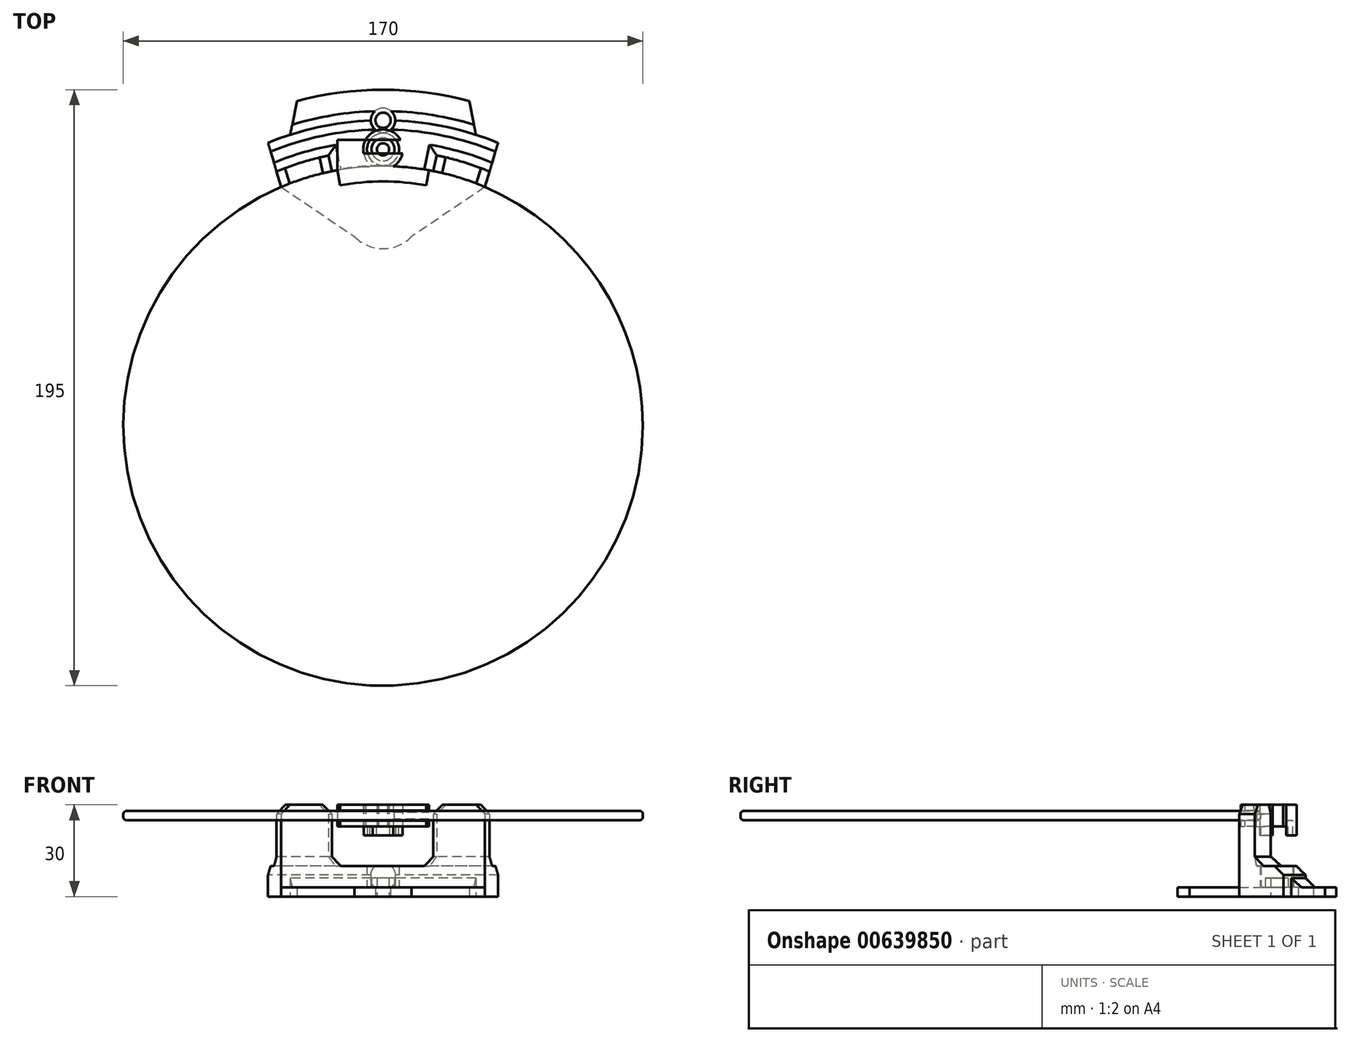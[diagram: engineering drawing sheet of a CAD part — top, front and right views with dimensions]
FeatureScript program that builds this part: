
annotation { "Feature Type Name" : "Feature", "Feature Type Description" : "" }
export const myFeature = defineFeature(function(context is Context, id is Id, definition is map)
    precondition{}
    {
        {
            var Q0;
            Q0=qCreatedBy(makeId("Top.planeOp"),FACE);
            var sketch = newSketch(context, id + "F0", { "sketchPlane" : qUnion([Q0])});
            skCircle(sketch, "E0", {"center": v(0, 0) * mm, "radius": 85 * mm});
            skLineSegment(sketch, "E1", {"start": v(0, 85) * mm, "end": v(0, 0) * mm, "construction": true});
            skLineSegment(sketch, "E2", {"start": v(0, 0) * mm, "end": v(-73.61, -42.5) * mm, "construction": true});
            skLineSegment(sketch, "E3", {"start": v(0, 0) * mm, "end": v(73.61, -42.5) * mm, "construction": true});
            skCircle(sketch, "E4", {"center": v(0, 100) * mm, "radius": 2.5 * mm});
            skCircle(sketch, "E5", {"center": v(0, 0) * mm, "radius": 100 * mm});
            skCircle(sketch, "E6", {"center": v(0, 0) * mm, "radius": 110 * mm});
            skCircle(sketch, "E7", {"center": v(0, 100) * mm, "radius": 4 * mm});
            skCircle(sketch, "E8", {"center": v(0, 71) * mm, "radius": 13 * mm});
            skCircle(sketch, "E9", {"center": v(0, 71) * mm, "radius": 9.5 * mm});
            skLineSegment(sketch, "E10", {"start": v(-37.65, 92.64) * mm, "end": v(-33.33, 78.2) * mm});
            skLineSegment(sketch, "E11", {"start": v(-33.33, 78.2) * mm, "end": v(-9.32, 61.94) * mm});
            skLineSegment(sketch, "E12", {"start": v(-30.4, 95.27) * mm, "end": v(-28.21, 106.32) * mm});
            skLineSegment(sketch, "E13.MirrorCS", {"start": v(33.33, 78.2) * mm, "end": v(9.32, 61.94) * mm});
            skLineSegment(sketch, "E14.MirrorCS", {"start": v(37.65, 92.64) * mm, "end": v(33.33, 78.2) * mm});
            skLineSegment(sketch, "E15.MirrorCS", {"start": v(30.4, 95.27) * mm, "end": v(28.21, 106.32) * mm});
            skArc(sketch, "E16", {"start": v(34.84, 83.25) * mm, "mid": v(0, 90.24) * mm, "end": v(-34.84, 83.25) * mm});
            skLineSegment(sketch, "E17", {"start": v(17.54, 88.52) * mm, "end": v(16.45, 83.4) * mm});
            skLineSegment(sketch, "E18", {"start": v(0, 85) * mm, "end": v(0, 116.4) * mm, "construction": true});
            skLineSegment(sketch, "E19", {"start": v(-17.83, 88.46) * mm, "end": v(-16.74, 83.33) * mm});
            skSolve(sketch);
        }
        {
            var Q0;
            {var subQ4=sQuery(id+"F0.wireOp",EDGE,"E12");Q0=makeQuery(id+"F0.imprint","IMPRINT",FACE,{"disambiguationData":[TD([[makeQuery(id+"F0.imprint","IMPRINT",EDGE,{"derivedFrom":subQ4}),-1.0]])]});}
            var Q1;
            {var subQ0=sQuery(id+"F0.wireOp",EDGE,"E5");var subQ1=sQuery(id+"F0.wireOp",EDGE,"E4");var subQ2=makeQuery(id+"F0.imprint","INTERSECT",VERTEX,{"disambiguationData":[OD(0.0)],"derivedFrom":[subQ1,subQ0]});Q1=makeQuery(id+"F0.imprint","IMPRINT",FACE,{"disambiguationData":[TD([[makeQuery(id+"F0.imprint","IMPRINT",EDGE,{"disambiguationData":[TD([[subQ2,-1.0]])],"derivedFrom":subQ1}),-1.0]])]});}
            var Q2;
            {var subQ0=sQuery(id+"F0.wireOp",EDGE,"E5");var subQ1=sQuery(id+"F0.wireOp",EDGE,"E4");var subQ2=makeQuery(id+"F0.imprint","INTERSECT",VERTEX,{"disambiguationData":[OD(0.0)],"derivedFrom":[subQ1,subQ0]});Q2=makeQuery(id+"F0.imprint","IMPRINT",FACE,{"disambiguationData":[TD([[makeQuery(id+"F0.imprint","IMPRINT",EDGE,{"disambiguationData":[TD([[subQ2,1.0]])],"derivedFrom":subQ1}),-1.0]])]});}
            var Q3;
            {var subQ7=sQuery(id+"F0.wireOp",EDGE,"E10");Q3=makeQuery(id+"F0.imprint","IMPRINT",FACE,{"disambiguationData":[TD([[makeQuery(id+"F0.imprint","IMPRINT",EDGE,{"derivedFrom":subQ7}),1.0]])]});}
            var Q4;
            {var subQ0=sQuery(id+"F0.wireOp",EDGE,"E11");Q4=makeQuery(id+"F0.imprint","IMPRINT",FACE,{"disambiguationData":[TD([[makeQuery(id+"F0.imprint","IMPRINT",EDGE,{"derivedFrom":subQ0}),1.0]])]});}
            var Q5;
            Q5=makeQuery(id+"F0.imprint","IMPRINT",FACE,{"disambiguationData":[TD([[makeQuery(id+"F0.imprint","IMPRINT",EDGE,{"derivedFrom":sQuery(id+"F0.wireOp",EDGE,"E9")}),-1.0]])]});
            var Q6;
            Q6=makeQuery(id+"F0.imprint","IMPRINT",FACE,{"disambiguationData":[TD([[makeQuery(id+"F0.imprint","IMPRINT",EDGE,{"derivedFrom":sQuery(id+"F0.wireOp",EDGE,"E9")}),1.0]])]});
            var Q7;
            {var subQ7=sQuery(id+"F0.wireOp",EDGE,"E16");Q7=makeQuery(id+"F0.imprint","IMPRINT",FACE,{"disambiguationData":[TD([[makeQuery(id+"F0.imprint","IMPRINT",EDGE,{"derivedFrom":subQ7}),-1.0]])]});}
            extrude(context, id + "F1", {"entities" : qUnion([Q0, Q1, Q2, Q3, Q4, Q5, Q6, Q7]), "depth" : 3 * mm, "offsetDistance" : 25 * mm});
        }
        {
            var Q0;
            {var subQ7=sQuery(id+"F0.wireOp",EDGE,"E10");Q0=makeQuery(id+"F0.imprint","IMPRINT",FACE,{"disambiguationData":[TD([[makeQuery(id+"F0.imprint","IMPRINT",EDGE,{"derivedFrom":subQ7}),1.0]])]});}
            var Q1;
            {var subQ7=sQuery(id+"F0.wireOp",EDGE,"E16");Q1=makeQuery(id+"F0.imprint","IMPRINT",FACE,{"disambiguationData":[TD([[makeQuery(id+"F0.imprint","IMPRINT",EDGE,{"derivedFrom":subQ7}),-1.0]])]});}
            var Q2;
            {var subQ0=sQuery(id+"F0.wireOp",EDGE,"E17");Q2=makeQuery(id+"F0.imprint","IMPRINT",FACE,{"disambiguationData":[TD([[makeQuery(id+"F0.imprint","IMPRINT",EDGE,{"derivedFrom":subQ0}),-1.0]])]});}
            var Q3;
            {var subQ3=sQuery(id+"F0.wireOp",EDGE,"E17");Q3=makeQuery(id+"F0.imprint","IMPRINT",FACE,{"disambiguationData":[TD([[makeQuery(id+"F0.imprint","IMPRINT",EDGE,{"derivedFrom":subQ3}),1.0]])]});}
            extrude(context, id + "F2", {"entities" : qUnion([Q0, Q1, Q2, Q3]), "operationType" : NewBodyOperationType.ADD, "depth" : 10 * mm, "offsetDistance" : 25 * mm});
        }
        {
            var Q0;
            {var subQ3=sQuery(id+"F0.wireOp",EDGE,"E17");Q0=makeQuery(id+"F0.imprint","IMPRINT",FACE,{"disambiguationData":[TD([[makeQuery(id+"F0.imprint","IMPRINT",EDGE,{"derivedFrom":subQ3}),1.0]])]});}
            var Q1;
            {var subQ3=sQuery(id+"F0.wireOp",EDGE,"E19");Q1=makeQuery(id+"F0.imprint","IMPRINT",FACE,{"disambiguationData":[TD([[makeQuery(id+"F0.imprint","IMPRINT",EDGE,{"derivedFrom":subQ3}),-1.0]])]});}
            extrude(context, id + "F3", {"entities" : qUnion([Q0, Q1]), "operationType" : NewBodyOperationType.ADD, "depth" : 30 * mm, "offsetDistance" : 25 * mm});
        }
        {
            var Q0;
            Q0=qCreatedBy(makeId("Top.planeOp"),FACE);
            cPlane(context, id + "F4", {"entities" : qUnion([Q0]), "cplaneType" : CPlaneType.OFFSET, "offset" : 25 * mm, "width" : 150 * mm, "height" : 150 * mm});
        }
        {
            var Q0;
            Q0=qCreatedBy(id+"F4.planeOp",FACE);
            var sketch = newSketch(context, id + "F5", { "sketchPlane" : qUnion([Q0])});
            skLineSegment(sketch, "E20.top", {"start": v(15, 89.17) * mm, "end": v(-15, 89.17) * mm});
            skPoint(sketch, "E20.middle", {"position": v(0, 85) * mm});
            skArc(sketch, "E21", {"start": v(15, 83.67) * mm, "mid": v(0, 85) * mm, "end": v(-15, 83.67) * mm});
            skArc(sketch, "E22", {"start": v(-15, 83.67) * mm, "mid": v(0, -85) * mm, "end": v(15, 83.67) * mm});
            skLineSegment(sketch, "E23.bottom", {"start": v(-15, 89.17) * mm, "end": v(14.83, 89.17) * mm});
            skLineSegment(sketch, "E23.top", {"start": v(-15, 93.56) * mm, "end": v(14.83, 93.56) * mm});
            skLineSegment(sketch, "E23.left", {"start": v(-15, 89.17) * mm, "end": v(-15, 93.56) * mm});
            skArc(sketch, "E24.0", {"start": v(14.12, 78.74) * mm, "mid": v(0, 80) * mm, "end": v(-14.12, 78.74) * mm});
            skLineSegment(sketch, "E25", {"start": v(-15, 89.17) * mm, "end": v(-15, 83.67) * mm});
            skLineSegment(sketch, "E26", {"start": v(-15, 83.67) * mm, "end": v(-14.12, 78.74) * mm});
            skLineSegment(sketch, "E27", {"start": v(14.12, 78.74) * mm, "end": v(15, 83.67) * mm});
            skLineSegment(sketch, "E28", {"start": v(15, 83.67) * mm, "end": v(15, 89.17) * mm});
            skLineSegment(sketch, "E29", {"start": v(0, 85) * mm, "end": v(0, 93.56) * mm, "construction": true});
            skPoint(sketch, "E29.endSnap0", {"position": v(0, 89.17) * mm});
            skLineSegment(sketch, "E30", {"start": v(14.83, 93.56) * mm, "end": v(15, 93.56) * mm});
            skLineSegment(sketch, "E31", {"start": v(15, 93.56) * mm, "end": v(15, 89.17) * mm});
            skCircle(sketch, "E32", {"center": v(0, 90.5) * mm, "radius": 5.25 * mm});
            skCircle(sketch, "E33", {"center": v(0, 90.5) * mm, "radius": 3.75 * mm});
            skCircle(sketch, "E34", {"center": v(0, 90.5) * mm, "radius": 2 * mm});
            skArc(sketch, "E35", {"start": v(5.74, 93.56) * mm, "mid": v(0, 97) * mm, "end": v(-5.74, 93.56) * mm});
            skArc(sketch, "E36", {"start": v(-5.74, 93.56) * mm, "mid": v(0, 84) * mm, "end": v(5.74, 93.56) * mm});
            skSolve(sketch);
        }
        {
            var Q0;
            Q0=makeQuery(id+"F5.imprint","IMPRINT",FACE,{"disambiguationData":[TD([[makeQuery(id+"F5.imprint","IMPRINT",EDGE,{"derivedFrom":sQuery(id+"F5.wireOp",EDGE,"E22")}),1.0]])]});
            var Q1;
            Q1=makeQuery(id+"F5.imprint","IMPRINT",FACE,{"disambiguationData":[TD([[makeQuery(id+"F5.imprint","IMPRINT",EDGE,{"derivedFrom":sQuery(id+"F5.wireOp",EDGE,"E21")}),1.0]])]});
            var Q2;
            {var subQ0=sQuery(id+"F5.wireOp",EDGE,"E36");var subQ1=sQuery(id+"F5.wireOp",EDGE,"E21");var subQ2=makeQuery(id+"F5.imprint","INTERSECT",VERTEX,{"disambiguationData":[OD(0.0)],"derivedFrom":[subQ1,subQ0]});Q2=makeQuery(id+"F5.imprint","IMPRINT",FACE,{"disambiguationData":[TD([[makeQuery(id+"F5.imprint","IMPRINT",EDGE,{"disambiguationData":[TD([[subQ2,-1.0]])],"derivedFrom":subQ1}),1.0]])]});}
            extrude(context, id + "F6", {"entities" : qUnion([Q0, Q1, Q2]), "depth" : 3 * mm, "offsetDistance" : 25 * mm});
        }
        {
            var Q0;
            Q0=makeQuery(id+"F6.opExtrude","SWEPT_FACE",FACE,{"disambiguationData":[OSD([sQuery(id+"F5.wireOp",EDGE,"E21"),sQuery(id+"F5.wireOp",EDGE,"E22")])]});
            fillet(context, id + "F7", {"entities" : qUnion([Q0]), "radius" : 1 * mm, "tangentPropagation" : true, "allowEdgeOverflow" : false});
        }
        {
            var Q0;
            {var subQ0=sQuery(id+"F5.wireOp",EDGE,"E23.left");Q0=makeQuery(id+"F5.imprint","IMPRINT",FACE,{"disambiguationData":[TD([[makeQuery(id+"F5.imprint","IMPRINT",EDGE,{"derivedFrom":subQ0}),-1.0]])]});}
            var Q1;
            {var subQ0=sQuery(id+"F5.wireOp",EDGE,"E32");var subQ1=sQuery(id+"F5.wireOp",EDGE,"E23.bottom");var subQ2=makeQuery(id+"F5.imprint","INTERSECT",VERTEX,{"disambiguationData":[OD(0.0)],"derivedFrom":[subQ1,subQ0]});Q1=makeQuery(id+"F5.imprint","IMPRINT",FACE,{"disambiguationData":[TD([[makeQuery(id+"F5.imprint","IMPRINT",EDGE,{"disambiguationData":[TD([[subQ2,-1.0]])],"derivedFrom":subQ1}),1.0]])]});}
            var Q2;
            {var subQ0=sQuery(id+"F5.wireOp",EDGE,"E33");var subQ1=sQuery(id+"F5.wireOp",EDGE,"E23.bottom");var subQ2=makeQuery(id+"F5.imprint","INTERSECT",VERTEX,{"disambiguationData":[OD(1.0)],"derivedFrom":[subQ1,subQ0]});Q2=makeQuery(id+"F5.imprint","IMPRINT",FACE,{"disambiguationData":[TD([[makeQuery(id+"F5.imprint","IMPRINT",EDGE,{"disambiguationData":[TD([[subQ2,-1.0]])],"derivedFrom":subQ1}),1.0]])]});}
            var Q3;
            Q3=makeQuery(id+"F5.imprint","IMPRINT",FACE,{"disambiguationData":[TD([[makeQuery(id+"F5.imprint","IMPRINT",EDGE,{"derivedFrom":sQuery(id+"F5.wireOp",EDGE,"E21")}),1.0]])]});
            var Q4;
            {var subQ0=sQuery(id+"F5.wireOp",EDGE,"E32");var subQ1=sQuery(id+"F5.wireOp",EDGE,"E23.bottom");var subQ2=makeQuery(id+"F5.imprint","INTERSECT",VERTEX,{"disambiguationData":[OD(0.0)],"derivedFrom":[subQ1,subQ0]});Q4=makeQuery(id+"F5.imprint","IMPRINT",FACE,{"disambiguationData":[TD([[makeQuery(id+"F5.imprint","IMPRINT",EDGE,{"disambiguationData":[TD([[subQ2,-1.0]])],"derivedFrom":subQ1}),-1.0]])]});}
            var Q5;
            {var subQ5=sQuery(id+"F5.wireOp",EDGE,"E20.top");Q5=makeQuery(id+"F5.imprint","IMPRINT",FACE,{"disambiguationData":[TD([[makeQuery(id+"F5.imprint","IMPRINT",EDGE,{"derivedFrom":subQ5}),-1.0]])]});}
            var Q6;
            {var subQ1=sQuery(id+"F5.wireOp",EDGE,"E20.top");Q6=makeQuery(id+"F5.imprint","IMPRINT",FACE,{"disambiguationData":[TD([[makeQuery(id+"F5.imprint","IMPRINT",EDGE,{"derivedFrom":subQ1}),1.0]])]});}
            var Q7;
            {var subQ0=sQuery(id+"F5.wireOp",EDGE,"E32");var subQ1=sQuery(id+"F5.wireOp",EDGE,"E23.top");var subQ2=makeQuery(id+"F5.imprint","INTERSECT",VERTEX,{"disambiguationData":[OD(0.0)],"derivedFrom":[subQ1,subQ0]});Q7=makeQuery(id+"F5.imprint","IMPRINT",FACE,{"disambiguationData":[TD([[makeQuery(id+"F5.imprint","IMPRINT",EDGE,{"disambiguationData":[TD([[subQ2,-1.0]])],"derivedFrom":subQ1}),1.0]])]});}
            var Q8;
            {var subQ0=sQuery(id+"F5.wireOp",EDGE,"E33");var subQ1=sQuery(id+"F5.wireOp",EDGE,"E23.bottom");var subQ2=makeQuery(id+"F5.imprint","INTERSECT",VERTEX,{"disambiguationData":[OD(0.0)],"derivedFrom":[subQ1,subQ0]});Q8=makeQuery(id+"F5.imprint","IMPRINT",FACE,{"disambiguationData":[TD([[makeQuery(id+"F5.imprint","IMPRINT",EDGE,{"disambiguationData":[TD([[subQ2,-1.0]])],"derivedFrom":subQ1}),1.0]])]});}
            var Q9;
            {var subQ0=sQuery(id+"F5.wireOp",EDGE,"E33");var subQ1=sQuery(id+"F5.wireOp",EDGE,"E23.bottom");var subQ2=makeQuery(id+"F5.imprint","INTERSECT",VERTEX,{"disambiguationData":[OD(0.0)],"derivedFrom":[subQ1,subQ0]});Q9=makeQuery(id+"F5.imprint","IMPRINT",FACE,{"disambiguationData":[TD([[makeQuery(id+"F5.imprint","IMPRINT",EDGE,{"disambiguationData":[TD([[subQ2,-1.0]])],"derivedFrom":subQ1}),-1.0]])]});}
            var Q10;
            {var subQ0=sQuery(id+"F5.wireOp",EDGE,"E33");var subQ1=sQuery(id+"F5.wireOp",EDGE,"E23.top");var subQ2=makeQuery(id+"F5.imprint","INTERSECT",VERTEX,{"disambiguationData":[OD(0.0)],"derivedFrom":[subQ1,subQ0]});Q10=makeQuery(id+"F5.imprint","IMPRINT",FACE,{"disambiguationData":[TD([[makeQuery(id+"F5.imprint","IMPRINT",EDGE,{"disambiguationData":[TD([[subQ2,-1.0]])],"derivedFrom":subQ1}),1.0]])]});}
            var Q11;
            {var subQ0=sQuery(id+"F5.wireOp",EDGE,"E35");Q11=makeQuery(id+"F5.imprint","IMPRINT",FACE,{"disambiguationData":[TD([[makeQuery(id+"F5.imprint","IMPRINT",EDGE,{"derivedFrom":subQ0}),1.0]])]});}
            var Q12;
            {var subQ0=sQuery(id+"F5.wireOp",EDGE,"E25");Q12=makeQuery(id+"F5.imprint","IMPRINT",FACE,{"disambiguationData":[TD([[makeQuery(id+"F5.imprint","IMPRINT",EDGE,{"derivedFrom":subQ0}),1.0]])]});}
            var Q13;
            {var subQ0=sQuery(id+"F5.wireOp",EDGE,"E36");var subQ1=sQuery(id+"F5.wireOp",EDGE,"E21");var subQ2=makeQuery(id+"F5.imprint","INTERSECT",VERTEX,{"disambiguationData":[OD(0.0)],"derivedFrom":[subQ1,subQ0]});Q13=makeQuery(id+"F5.imprint","IMPRINT",FACE,{"disambiguationData":[TD([[makeQuery(id+"F5.imprint","IMPRINT",EDGE,{"disambiguationData":[TD([[subQ2,-1.0]])],"derivedFrom":subQ1}),1.0]])]});}
            var Q14;
            {var subQ4=sQuery(id+"F5.wireOp",EDGE,"E36");var subQ7=sQuery(id+"F5.wireOp",EDGE,"E21");var subQ8=makeQuery(id+"F5.imprint","INTERSECT",VERTEX,{"disambiguationData":[OD(0.0)],"derivedFrom":[subQ7,subQ4]});Q14=makeQuery(id+"F5.imprint","IMPRINT",FACE,{"disambiguationData":[TD([[makeQuery(id+"F5.imprint","IMPRINT",EDGE,{"disambiguationData":[TD([[subQ8,-1.0]])],"derivedFrom":subQ7}),-1.0]])]});}
            var Q15;
            {var subQ0=sQuery(id+"F5.wireOp",EDGE,"E36");var subQ1=sQuery(id+"F5.wireOp",EDGE,"E23.bottom");var subQ2=makeQuery(id+"F5.imprint","INTERSECT",VERTEX,{"disambiguationData":[OD(0.0)],"derivedFrom":[subQ1,subQ0]});Q15=makeQuery(id+"F5.imprint","IMPRINT",FACE,{"disambiguationData":[TD([[makeQuery(id+"F5.imprint","IMPRINT",EDGE,{"disambiguationData":[TD([[subQ2,-1.0]])],"derivedFrom":subQ1}),1.0]])]});}
            var Q16;
            {var subQ0=sQuery(id+"F5.wireOp",EDGE,"E32");var subQ1=sQuery(id+"F5.wireOp",EDGE,"E23.bottom");var subQ2=makeQuery(id+"F5.imprint","INTERSECT",VERTEX,{"disambiguationData":[OD(1.0)],"derivedFrom":[subQ1,subQ0]});Q16=makeQuery(id+"F5.imprint","IMPRINT",FACE,{"disambiguationData":[TD([[makeQuery(id+"F5.imprint","IMPRINT",EDGE,{"disambiguationData":[TD([[subQ2,-1.0]])],"derivedFrom":subQ1}),1.0]])]});}
            extrude(context, id + "F8", {"entities" : qUnion([Q0, Q1, Q2, Q3, Q4, Q5, Q6, Q7, Q8, Q9, Q10, Q11, Q12, Q13, Q14, Q15, Q16]), "depth" : 5 * mm, "offsetDistance" : 25 * mm, "hasSecondDirection" : true, "secondDirectionOppositeDirection" : true, "secondDirectionDepth" : 2 * mm});
        }
        {
            var Q0;
            {var subQ0=sQuery(id+"F5.wireOp",EDGE,"E32");var subQ1=sQuery(id+"F5.wireOp",EDGE,"E23.top");var subQ2=makeQuery(id+"F5.imprint","INTERSECT",VERTEX,{"disambiguationData":[OD(0.0)],"derivedFrom":[subQ1,subQ0]});Q0=makeQuery(id+"F5.imprint","IMPRINT",FACE,{"disambiguationData":[TD([[makeQuery(id+"F5.imprint","IMPRINT",EDGE,{"disambiguationData":[TD([[subQ2,-1.0]])],"derivedFrom":subQ1}),1.0]])]});}
            var Q1;
            {var subQ0=sQuery(id+"F5.wireOp",EDGE,"E33");var subQ1=sQuery(id+"F5.wireOp",EDGE,"E23.bottom");var subQ2=makeQuery(id+"F5.imprint","INTERSECT",VERTEX,{"disambiguationData":[OD(1.0)],"derivedFrom":[subQ1,subQ0]});Q1=makeQuery(id+"F5.imprint","IMPRINT",FACE,{"disambiguationData":[TD([[makeQuery(id+"F5.imprint","IMPRINT",EDGE,{"disambiguationData":[TD([[subQ2,-1.0]])],"derivedFrom":subQ1}),1.0]])]});}
            var Q2;
            {var subQ0=sQuery(id+"F5.wireOp",EDGE,"E32");var subQ1=sQuery(id+"F5.wireOp",EDGE,"E23.bottom");var subQ2=makeQuery(id+"F5.imprint","INTERSECT",VERTEX,{"disambiguationData":[OD(0.0)],"derivedFrom":[subQ1,subQ0]});Q2=makeQuery(id+"F5.imprint","IMPRINT",FACE,{"disambiguationData":[TD([[makeQuery(id+"F5.imprint","IMPRINT",EDGE,{"disambiguationData":[TD([[subQ2,-1.0]])],"derivedFrom":subQ1}),-1.0]])]});}
            var Q3;
            {var subQ0=sQuery(id+"F5.wireOp",EDGE,"E32");var subQ1=sQuery(id+"F5.wireOp",EDGE,"E23.bottom");var subQ2=makeQuery(id+"F5.imprint","INTERSECT",VERTEX,{"disambiguationData":[OD(0.0)],"derivedFrom":[subQ1,subQ0]});Q3=makeQuery(id+"F5.imprint","IMPRINT",FACE,{"disambiguationData":[TD([[makeQuery(id+"F5.imprint","IMPRINT",EDGE,{"disambiguationData":[TD([[subQ2,-1.0]])],"derivedFrom":subQ1}),1.0]])]});}
            extrude(context, id + "F9", {"entities" : qUnion([Q0, Q1, Q2, Q3]), "operationType" : NewBodyOperationType.REMOVE, "oppositeDirection" : true, "depth" : 5 * mm, "offsetDistance" : 25 * mm});
        }
        {
            var Q0;
            {var subQ0=sQuery(id+"F5.wireOp",EDGE,"E32");var subQ1=sQuery(id+"F5.wireOp",EDGE,"E23.bottom");var subQ2=makeQuery(id+"F5.imprint","INTERSECT",VERTEX,{"disambiguationData":[OD(1.0)],"derivedFrom":[subQ1,subQ0]});Q0=makeQuery(id+"F5.imprint","IMPRINT",FACE,{"disambiguationData":[TD([[makeQuery(id+"F5.imprint","IMPRINT",EDGE,{"disambiguationData":[TD([[subQ2,-1.0]])],"derivedFrom":subQ1}),1.0]])]});}
            var Q1;
            {var subQ1=sQuery(id+"F5.wireOp",EDGE,"E35");Q1=makeQuery(id+"F5.imprint","IMPRINT",FACE,{"disambiguationData":[TD([[makeQuery(id+"F5.imprint","IMPRINT",EDGE,{"derivedFrom":subQ1}),1.0]])]});}
            var Q2;
            {var subQ0=sQuery(id+"F5.wireOp",EDGE,"E36");var subQ1=sQuery(id+"F5.wireOp",EDGE,"E23.bottom");var subQ2=makeQuery(id+"F5.imprint","INTERSECT",VERTEX,{"disambiguationData":[OD(0.0)],"derivedFrom":[subQ1,subQ0]});Q2=makeQuery(id+"F5.imprint","IMPRINT",FACE,{"disambiguationData":[TD([[makeQuery(id+"F5.imprint","IMPRINT",EDGE,{"disambiguationData":[TD([[subQ2,-1.0]])],"derivedFrom":subQ1}),1.0]])]});}
            var Q3;
            {var subQ4=sQuery(id+"F5.wireOp",EDGE,"E36");var subQ7=sQuery(id+"F5.wireOp",EDGE,"E21");var subQ8=makeQuery(id+"F5.imprint","INTERSECT",VERTEX,{"disambiguationData":[OD(0.0)],"derivedFrom":[subQ7,subQ4]});Q3=makeQuery(id+"F5.imprint","IMPRINT",FACE,{"disambiguationData":[TD([[makeQuery(id+"F5.imprint","IMPRINT",EDGE,{"disambiguationData":[TD([[subQ8,-1.0]])],"derivedFrom":subQ7}),-1.0]])]});}
            var Q4;
            {var subQ0=sQuery(id+"F5.wireOp",EDGE,"E33");var subQ1=sQuery(id+"F5.wireOp",EDGE,"E23.bottom");var subQ2=makeQuery(id+"F5.imprint","INTERSECT",VERTEX,{"disambiguationData":[OD(0.0)],"derivedFrom":[subQ1,subQ0]});Q4=makeQuery(id+"F5.imprint","IMPRINT",FACE,{"disambiguationData":[TD([[makeQuery(id+"F5.imprint","IMPRINT",EDGE,{"disambiguationData":[TD([[subQ2,-1.0]])],"derivedFrom":subQ1}),-1.0]])]});}
            var Q5;
            {var subQ0=sQuery(id+"F5.wireOp",EDGE,"E33");var subQ1=sQuery(id+"F5.wireOp",EDGE,"E23.bottom");var subQ2=makeQuery(id+"F5.imprint","INTERSECT",VERTEX,{"disambiguationData":[OD(0.0)],"derivedFrom":[subQ1,subQ0]});Q5=makeQuery(id+"F5.imprint","IMPRINT",FACE,{"disambiguationData":[TD([[makeQuery(id+"F5.imprint","IMPRINT",EDGE,{"disambiguationData":[TD([[subQ2,-1.0]])],"derivedFrom":subQ1}),1.0]])]});}
            var Q6;
            {var subQ0=sQuery(id+"F5.wireOp",EDGE,"E33");var subQ1=sQuery(id+"F5.wireOp",EDGE,"E23.top");var subQ2=makeQuery(id+"F5.imprint","INTERSECT",VERTEX,{"disambiguationData":[OD(0.0)],"derivedFrom":[subQ1,subQ0]});Q6=makeQuery(id+"F5.imprint","IMPRINT",FACE,{"disambiguationData":[TD([[makeQuery(id+"F5.imprint","IMPRINT",EDGE,{"disambiguationData":[TD([[subQ2,-1.0]])],"derivedFrom":subQ1}),1.0]])]});}
            extrude(context, id + "F10", {"entities" : qUnion([Q0, Q1, Q2, Q3, Q4, Q5, Q6]), "operationType" : NewBodyOperationType.ADD, "oppositeDirection" : true, "depth" : 5 * mm, "offsetDistance" : 25 * mm});
        }
        {
            var Q0;
            Q0=makeQuery(id+"F6.opExtrude","SWEPT_BODY",BODY,{"disambiguationData":[OSD([sQuery(id+"F5.wireOp",EDGE,"E21"),sQuery(id+"F5.wireOp",EDGE,"E22")])]});
            var Q1;
            Q1=makeQuery(id+"F8.opExtrude","SWEPT_BODY",BODY,{"disambiguationData":[OSD([sQuery(id+"F5.wireOp",EDGE,"E20.bottom"),sQuery(id+"F5.wireOp",EDGE,"E20.top"),sQuery(id+"F5.wireOp",EDGE,"E20.left"),sQuery(id+"F5.wireOp",EDGE,"E20.right"),sQuery(id+"F5.wireOp",EDGE,"659e0c46-0fa9-4924-868b-f0d8e4e3b63c.0"),sQuery(id+"F5.wireOp",EDGE,"d0e39e6c-d1af-4c3a-9b0b-4ca04ba41e75.trimOffspring"),sQuery(id+"F5.wireOp",EDGE,"E23.top"),sQuery(id+"F5.wireOp",EDGE,"E23.left"),sQuery(id+"F5.wireOp",EDGE,"E23.right")])]});
            booleanBodies(context, id + "F11", {"operationType" : BooleanOperationType.SUBTRACTION, "tools" : qUnion([Q0]), "targets" : qUnion([Q1]), "offset" : true, "offsetAll" : true, "offsetDistance" : .2 * mm, "keepTools" : true});
        }
        {
            var Q0;
            Q0=qCreatedBy(makeId("Top.planeOp"),FACE);
            var sketch = newSketch(context, id + "F12", { "sketchPlane" : qUnion([Q0])});
            skArc(sketch, "E37.0", {"start": v(-5.74, 93.56) * mm, "mid": v(0, 84) * mm, "end": v(5.74, 93.56) * mm});
            skArc(sketch, "E37.1", {"start": v(5.74, 93.56) * mm, "mid": v(0, 97) * mm, "end": v(-5.74, 93.56) * mm});
            skCircle(sketch, "E37.2", {"center": v(0, 90.5) * mm, "radius": 5.25 * mm});
            skCircle(sketch, "E37.3", {"center": v(0, 90.5) * mm, "radius": 3.75 * mm});
            skCircle(sketch, "E37.4", {"center": v(0, 90.5) * mm, "radius": 2 * mm});
            skArc(sketch, "E38.0", {"start": v(4, 99.92) * mm, "mid": v(0, 96) * mm, "end": v(-4, 99.92) * mm});
            skArc(sketch, "E39.0", {"start": v(-33.33, 78.2) * mm, "mid": v(0, 85) * mm, "end": v(33.33, 78.2) * mm});
            skSolve(sketch);
        }
        {
            var Q0;
            Q0=makeQuery(id+"F12.imprint","IMPRINT",FACE,{"disambiguationData":[TD([[makeQuery(id+"F12.imprint","IMPRINT",EDGE,{"derivedFrom":sQuery(id+"F12.wireOp",EDGE,"E37.0")}),1.0]])]});
            var Q1;
            Q1=makeQuery(id+"F12.imprint","IMPRINT",FACE,{"disambiguationData":[TD([[makeQuery(id+"F12.imprint","IMPRINT",EDGE,{"derivedFrom":sQuery(id+"F12.wireOp",EDGE,"E37.3")}),1.0]])]});
            extrude(context, id + "F13", {"entities" : qUnion([Q0, Q1]), "operationType" : NewBodyOperationType.ADD, "depth" : 11 * mm, "offsetDistance" : 25 * mm});
        }
        {
            var Q0;
            Q0=makeQuery(id+"F13.boolean.opBoolean","SPLIT",FACE,{"disambiguationData":[TD([makeQuery(id+"F13.opExtrude","SWEPT_FACE",FACE,{"disambiguationData":[OSD([sQuery(id+"F12.wireOp",EDGE,"E37.2")])]})])],"derivedFrom":makeQuery(id+"F2.opExtrude","CAP_FACE",FACE,{"disambiguationData":[OSD([sQuery(id+"F0.wireOp",EDGE,"E0"),sQuery(id+"F0.wireOp",EDGE,"E5"),sQuery(id+"F0.wireOp",EDGE,"E7"),sQuery(id+"F0.wireOp",EDGE,"E10"),sQuery(id+"F0.wireOp",EDGE,"E14.MirrorCS")])],"isStart":false})});
            extrude(context, id + "F14", {"entities" : qUnion([Q0]), "operationType" : NewBodyOperationType.REMOVE, "oppositeDirection" : true, "depth" : 7 * mm, "offsetDistance" : 25 * mm});
        }
        {
            var Q0;
            Q0=makeQuery(id+"F13.boolean.opBoolean","SPLIT",FACE,{"disambiguationData":[TD([makeQuery(id+"F13.opExtrude","SWEPT_FACE",FACE,{"disambiguationData":[OSD([sQuery(id+"F12.wireOp",EDGE,"E37.4")])]})])],"derivedFrom":makeQuery(id+"F2.opExtrude","CAP_FACE",FACE,{"disambiguationData":[OSD([sQuery(id+"F0.wireOp",EDGE,"E0"),sQuery(id+"F0.wireOp",EDGE,"E5"),sQuery(id+"F0.wireOp",EDGE,"E7"),sQuery(id+"F0.wireOp",EDGE,"E10"),sQuery(id+"F0.wireOp",EDGE,"E14.MirrorCS")])],"isStart":false})});
            extrude(context, id + "F15", {"entities" : qUnion([Q0]), "operationType" : NewBodyOperationType.REMOVE, "oppositeDirection" : true, "depth" : 25 * mm, "offsetDistance" : 25 * mm});
        }
        {
            var Q0;
            Q0=makeQuery(id+"F13.opExtrude","CAP_FACE",FACE,{"disambiguationData":[OSD([sQuery(id+"F12.wireOp",EDGE,"E37.3"),sQuery(id+"F12.wireOp",EDGE,"E37.4")])],"isStart":false});
            extrude(context, id + "F16", {"entities" : qUnion([Q0]), "operationType" : NewBodyOperationType.REMOVE, "oppositeDirection" : true, "depth" : 5 * mm, "offsetDistance" : 25 * mm});
        }
        {
            var Q0;
            Q0=makeQuery(id+"F13.opExtrude","CAP_FACE",FACE,{"disambiguationData":[OSD([sQuery(id+"F12.wireOp",EDGE,"E37.0"),sQuery(id+"F12.wireOp",EDGE,"E37.1"),sQuery(id+"F12.wireOp",EDGE,"E37.2"),sQuery(id+"F12.wireOp",EDGE,"E38.0"),sQuery(id+"F12.wireOp",EDGE,"E39.0")])],"isStart":false});
            extrude(context, id + "F17", {"entities" : qUnion([Q0]), "operationType" : NewBodyOperationType.REMOVE, "oppositeDirection" : true, "depth" : 1 * mm, "offsetDistance" : 25 * mm});
        }
        {
            var Q0;
            Q0=makeQuery(id+"F3.boolean.opBoolean","INTERSECT",EDGE,{"derivedFrom":[makeQuery(id+"F2.opExtrude","CAP_FACE",FACE,{"disambiguationData":[OSD([sQuery(id+"F0.wireOp",EDGE,"E0"),sQuery(id+"F0.wireOp",EDGE,"E5"),sQuery(id+"F0.wireOp",EDGE,"E7"),sQuery(id+"F0.wireOp",EDGE,"E10"),sQuery(id+"F0.wireOp",EDGE,"E14.MirrorCS")])],"isStart":false}),makeQuery(id+"F3.opExtrude","SWEPT_FACE",FACE,{"disambiguationData":[OSD([sQuery(id+"F0.wireOp",EDGE,"E17")])]})]});
            var Q1;
            {var subQ0=sQuery(id+"F0.wireOp",EDGE,"E16");var subQ1=sQuery(id+"F0.wireOp",EDGE,"E14.MirrorCS");Q1=makeQuery(id+"F3.boolean.opBoolean","INTERSECT",EDGE,{"derivedFrom":[makeQuery(id+"F2.opExtrude","CAP_FACE",FACE,{"disambiguationData":[OSD([sQuery(id+"F0.wireOp",EDGE,"E0"),sQuery(id+"F0.wireOp",EDGE,"E5"),sQuery(id+"F0.wireOp",EDGE,"E7"),sQuery(id+"F0.wireOp",EDGE,"E10"),subQ1])],"isStart":false}),makeQuery(id+"F3.opExtrude","SWEPT_FACE",FACE,{"disambiguationData":[OSD([subQ0]),TDD([makeQuery(id+"F0.imprint","IMPRINT",EDGE,{"disambiguationData":[TD([[makeQuery(id+"F0.imprint","INTERSECT",VERTEX,{"derivedFrom":[subQ1,subQ0]}),-1.0]])],"derivedFrom":subQ0})])]})]});}
            var Q2;
            {var subQ0=sQuery(id+"F0.wireOp",EDGE,"E16");var subQ1=sQuery(id+"F0.wireOp",EDGE,"E10");Q2=makeQuery(id+"F3.boolean.opBoolean","INTERSECT",EDGE,{"derivedFrom":[makeQuery(id+"F2.opExtrude","CAP_FACE",FACE,{"disambiguationData":[OSD([sQuery(id+"F0.wireOp",EDGE,"E0"),sQuery(id+"F0.wireOp",EDGE,"E5"),sQuery(id+"F0.wireOp",EDGE,"E7"),subQ1,sQuery(id+"F0.wireOp",EDGE,"E14.MirrorCS")])],"isStart":false}),makeQuery(id+"F3.opExtrude","SWEPT_FACE",FACE,{"disambiguationData":[OSD([subQ0]),TDD([makeQuery(id+"F0.imprint","IMPRINT",EDGE,{"disambiguationData":[TD([[makeQuery(id+"F0.imprint","INTERSECT",VERTEX,{"derivedFrom":[subQ1,subQ0]}),1.0]])],"derivedFrom":subQ0})])]})]});}
            var Q3;
            Q3=makeQuery(id+"F3.boolean.opBoolean","INTERSECT",EDGE,{"derivedFrom":[makeQuery(id+"F2.opExtrude","CAP_FACE",FACE,{"disambiguationData":[OSD([sQuery(id+"F0.wireOp",EDGE,"E0"),sQuery(id+"F0.wireOp",EDGE,"E5"),sQuery(id+"F0.wireOp",EDGE,"E7"),sQuery(id+"F0.wireOp",EDGE,"E10"),sQuery(id+"F0.wireOp",EDGE,"E14.MirrorCS")])],"isStart":false}),makeQuery(id+"F3.opExtrude","SWEPT_FACE",FACE,{"disambiguationData":[OSD([sQuery(id+"F0.wireOp",EDGE,"E19")])]})]});
            var Q4;
            Q4=makeQuery(id+"F3.opExtrude","CAP_EDGE",EDGE,{"disambiguationData":[OSD([sQuery(id+"F0.wireOp",EDGE,"E17")])],"isStart":false});
            var Q5;
            Q5=makeQuery(id+"F3.opExtrude","CAP_EDGE",EDGE,{"disambiguationData":[OSD([sQuery(id+"F0.wireOp",EDGE,"E19")])],"isStart":false});
            var Q6;
            Q6=makeQuery(id+"F3.opExtrude","CAP_EDGE",EDGE,{"disambiguationData":[OSD([sQuery(id+"F0.wireOp",EDGE,"E14.MirrorCS")])],"isStart":false});
            var Q7;
            Q7=makeQuery(id+"F3.opExtrude","CAP_EDGE",EDGE,{"disambiguationData":[OSD([sQuery(id+"F0.wireOp",EDGE,"E10")])],"isStart":false});
            var Q8;
            {var subQ0=sQuery(id+"F0.wireOp",EDGE,"E5");var subQ1=makeQuery(id+"F0.imprint","INTERSECT",VERTEX,{"derivedFrom":[subQ0,sQuery(id+"F0.wireOp",EDGE,"E12")]});Q8=makeQuery(id+"F2.opExtrude","CAP_EDGE",EDGE,{"disambiguationData":[OSD([subQ0]),TDD([makeQuery(id+"F0.imprint","IMPRINT",EDGE,{"disambiguationData":[TD([[subQ1,1.0]])],"derivedFrom":subQ0}),makeQuery(id+"F0.imprint","IMPRINT",EDGE,{"disambiguationData":[TD([[makeQuery(id+"F0.imprint","INTERSECT",VERTEX,{"derivedFrom":[subQ0,sQuery(id+"F0.wireOp",EDGE,"E10")]}),1.0]])],"derivedFrom":subQ0})])],"isStart":false});}
            var Q9;
            {var subQ0=sQuery(id+"F0.wireOp",EDGE,"E5");var subQ1=makeQuery(id+"F0.imprint","INTERSECT",VERTEX,{"derivedFrom":[subQ0,sQuery(id+"F0.wireOp",EDGE,"E15.MirrorCS")]});Q9=makeQuery(id+"F2.opExtrude","CAP_EDGE",EDGE,{"disambiguationData":[OSD([subQ0]),TDD([makeQuery(id+"F0.imprint","IMPRINT",EDGE,{"disambiguationData":[TD([[makeQuery(id+"F0.imprint","INTERSECT",VERTEX,{"derivedFrom":[subQ0,sQuery(id+"F0.wireOp",EDGE,"E14.MirrorCS")]}),-1.0]])],"derivedFrom":subQ0}),makeQuery(id+"F0.imprint","IMPRINT",EDGE,{"disambiguationData":[TD([[subQ1,-1.0]])],"derivedFrom":subQ0})])],"isStart":false});}
            var Q10;
            {var subQ0=sQuery(id+"F0.wireOp",EDGE,"E15.MirrorCS");var subQ1=sQuery(id+"F0.wireOp",EDGE,"E5");var subQ2=makeQuery(id+"F0.imprint","INTERSECT",VERTEX,{"derivedFrom":[subQ1,subQ0]});var subQ3=sQuery(id+"F0.wireOp",EDGE,"E14.MirrorCS");Q10=makeQuery(id+"F2.boolean.opBoolean","INTERSECT",EDGE,{"derivedFrom":[makeQuery(id+"F1.opExtrude","CAP_FACE",FACE,{"disambiguationData":[OSD([sQuery(id+"F0.wireOp",EDGE,"E0"),sQuery(id+"F0.wireOp",EDGE,"E4"),subQ1,sQuery(id+"F0.wireOp",EDGE,"E8"),sQuery(id+"F0.wireOp",EDGE,"E10"),sQuery(id+"F0.wireOp",EDGE,"E11"),sQuery(id+"F0.wireOp",EDGE,"E12"),sQuery(id+"F0.wireOp",EDGE,"E13.MirrorCS"),subQ3,subQ0,sQuery(id+"F0.wireOp",EDGE,"E6"),sQuery(id+"F0.wireOp",EDGE,"E16"),sQuery(id+"F0.wireOp",EDGE,"E19")])],"isStart":false}),makeQuery(id+"F2.opExtrude","SWEPT_FACE",FACE,{"disambiguationData":[OSD([subQ1]),TDD([makeQuery(id+"F0.imprint","IMPRINT",EDGE,{"disambiguationData":[TD([[makeQuery(id+"F0.imprint","INTERSECT",VERTEX,{"derivedFrom":[subQ1,subQ3]}),-1.0]])],"derivedFrom":subQ1}),makeQuery(id+"F0.imprint","IMPRINT",EDGE,{"disambiguationData":[TD([[subQ2,-1.0]])],"derivedFrom":subQ1})])]})]});}
            var Q11;
            {var subQ0=sQuery(id+"F0.wireOp",EDGE,"E10");var subQ1=sQuery(id+"F0.wireOp",EDGE,"E5");var subQ2=sQuery(id+"F0.wireOp",EDGE,"E12");var subQ3=makeQuery(id+"F0.imprint","INTERSECT",VERTEX,{"derivedFrom":[subQ1,subQ2]});Q11=makeQuery(id+"F2.boolean.opBoolean","INTERSECT",EDGE,{"derivedFrom":[makeQuery(id+"F1.opExtrude","CAP_FACE",FACE,{"disambiguationData":[OSD([sQuery(id+"F0.wireOp",EDGE,"E0"),sQuery(id+"F0.wireOp",EDGE,"E4"),subQ1,sQuery(id+"F0.wireOp",EDGE,"E8"),subQ0,sQuery(id+"F0.wireOp",EDGE,"E11"),subQ2,sQuery(id+"F0.wireOp",EDGE,"E13.MirrorCS"),sQuery(id+"F0.wireOp",EDGE,"E14.MirrorCS"),sQuery(id+"F0.wireOp",EDGE,"E15.MirrorCS"),sQuery(id+"F0.wireOp",EDGE,"E6"),sQuery(id+"F0.wireOp",EDGE,"E16"),sQuery(id+"F0.wireOp",EDGE,"E19")])],"isStart":false}),makeQuery(id+"F2.opExtrude","SWEPT_FACE",FACE,{"disambiguationData":[OSD([subQ1]),TDD([makeQuery(id+"F0.imprint","IMPRINT",EDGE,{"disambiguationData":[TD([[subQ3,1.0]])],"derivedFrom":subQ1}),makeQuery(id+"F0.imprint","IMPRINT",EDGE,{"disambiguationData":[TD([[makeQuery(id+"F0.imprint","INTERSECT",VERTEX,{"derivedFrom":[subQ1,subQ0]}),1.0]])],"derivedFrom":subQ1})])]})]});}
            chamfer(context, id + "F18", {"entities" : qUnion([Q0, Q1, Q2, Q3, Q4, Q5, Q6, Q7, Q8, Q9, Q10, Q11]), "width" : 3 * mm, "tangentPropagation" : true});
        }
    });
